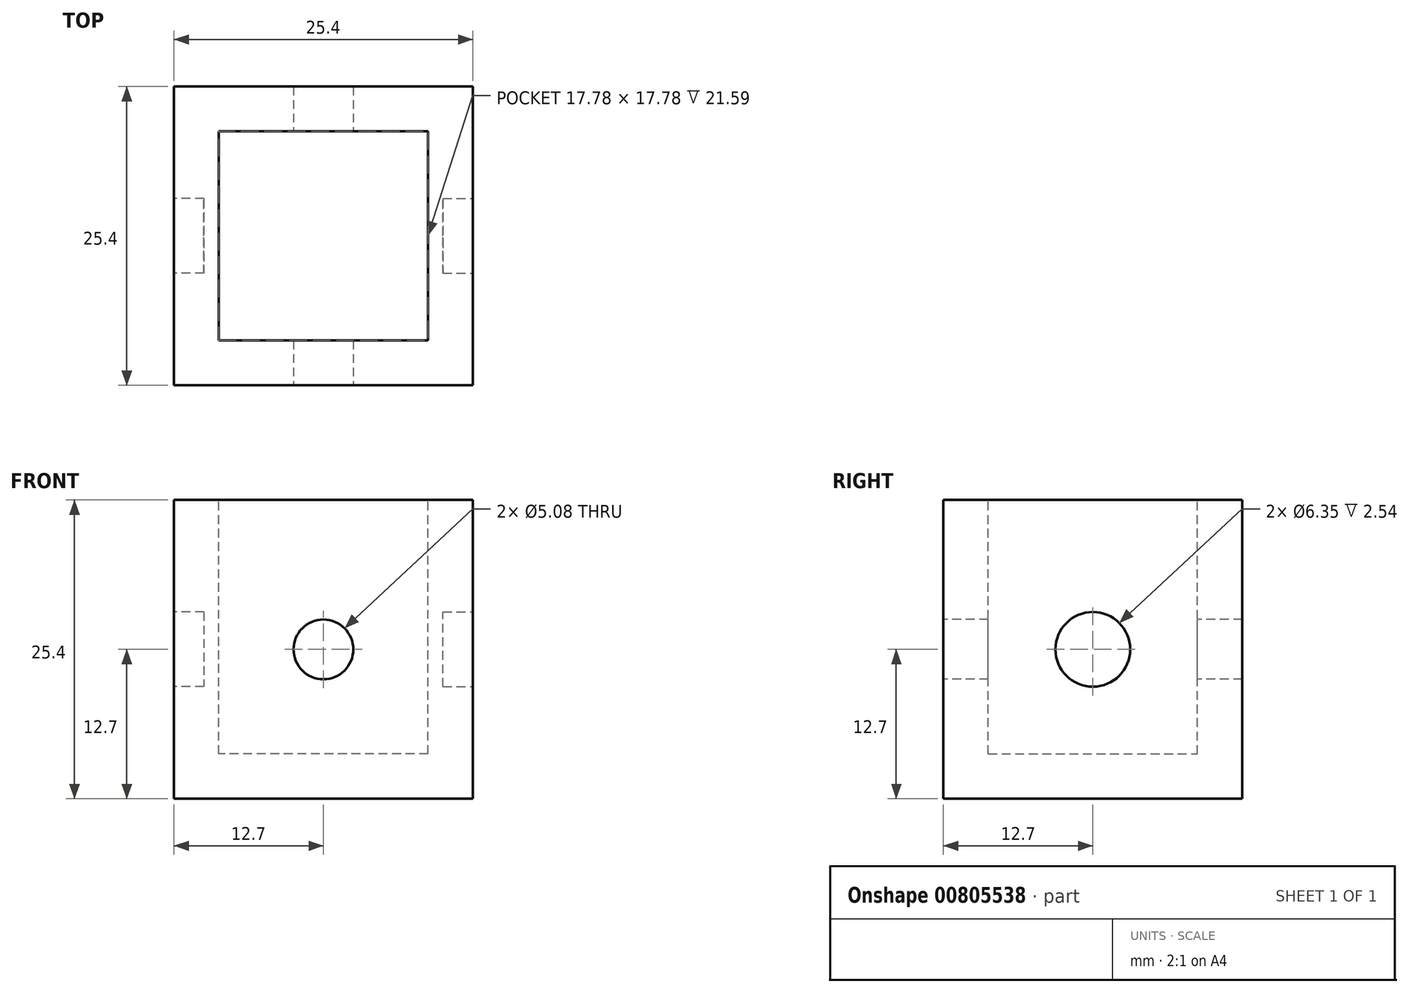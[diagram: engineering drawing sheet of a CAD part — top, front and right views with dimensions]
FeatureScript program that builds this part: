
annotation { "Feature Type Name" : "Feature", "Feature Type Description" : "" }
export const myFeature = defineFeature(function(context is Context, id is Id, definition is map)
    precondition{}
    {
        {
            var Q0;
            Q0=qCreatedBy(makeId("Front.planeOp"),FACE);
            var sketch = newSketch(context, id + "F0", { "sketchPlane" : qUnion([Q0])});
            skLineSegment(sketch, "E0.bottom", {"start": v(0, 0) * mm, "end": v(-25.4, 0) * mm});
            skLineSegment(sketch, "E0.top", {"start": v(0, 25.4) * mm, "end": v(-25.4, 25.4) * mm});
            skLineSegment(sketch, "E0.left", {"start": v(0, 0) * mm, "end": v(0, 25.4) * mm});
            skLineSegment(sketch, "E0.right", {"start": v(-25.4, 0) * mm, "end": v(-25.4, 25.4) * mm});
            skSolve(sketch);
        }
        {
            var Q0;
            Q0 = qSketchRegion(id + "F0", true);
            extrude(context, id + "F1", {"entities" : qUnion([Q0]), "depth" : 25.4 * mm, "offsetDistance" : 25.4 * mm});
        }
        {
            var Q0;
            Q0=makeQuery(id+"F1.opExtrude","SWEPT_FACE",FACE,{"disambiguationData":[OSD([sQuery(id+"F0.wireOp",EDGE,"E0.top")])]});
            shell(context, id + "F2", {"entities" : qUnion([Q0]), "thickness" : 3.8 * mm});
        }
        {
            var Q0;
            Q0=makeQuery(id+"F1.opExtrude","CAP_FACE",FACE,{"disambiguationData":[OSD([sQuery(id+"F0.wireOp",EDGE,"E0.bottom"),sQuery(id+"F0.wireOp",EDGE,"E0.top"),sQuery(id+"F0.wireOp",EDGE,"E0.left"),sQuery(id+"F0.wireOp",EDGE,"E0.right")])],"isStart":false});
            var sketch = newSketch(context, id + "F3", { "sketchPlane" : qUnion([Q0])});
            skPoint(sketch, "E1", {"position": v(-12.7, 12.7) * mm});
            skSolve(sketch);
        }
        {
            var Q0;
            Q0=makeQuery(id+"F1.opExtrude","SWEPT_FACE",FACE,{"disambiguationData":[OSD([sQuery(id+"F0.wireOp",EDGE,"E0.left")])]});
            var sketch = newSketch(context, id + "F4", { "sketchPlane" : qUnion([Q0])});
            skPoint(sketch, "E2", {"position": v(-12.7, 12.7) * mm});
            skCircle(sketch, "E3", {"center": v(-12.7, 12.7) * mm, "radius": 3.18 * mm});
            skSolve(sketch);
        }
        {
            var Q0;
            Q0=sQuery(id+"F3.wireOp",VERTEX,"E1");
            var Q1;
            Q1=makeQuery(id+"F1.opExtrude","SWEPT_BODY",BODY,{"disambiguationData":[OSD([sQuery(id+"F0.wireOp",EDGE,"E0.bottom"),sQuery(id+"F0.wireOp",EDGE,"E0.top"),sQuery(id+"F0.wireOp",EDGE,"E0.left"),sQuery(id+"F0.wireOp",EDGE,"E0.right")])]});
            hole(context, id + "F5", {"style" : HoleStyle.SIMPLE, "endStyle" : HoleEndStyle.BLIND, "holeDiameter" : 5.08 * mm, "majorDiameter" : 6.35 * mm, "holeDepth" : 50.8 * mm, "isTappedThrough" : true, "tappedDepth" : 12.7 * mm, "tapClearance" : 3, "startFromSketch" : true, "locations" : qUnion([Q0]), "scope" : qUnion([Q1])});
        }
        {
            var Q0;
            Q0=makeQuery(id+"F4.imprint","IMPRINT",FACE,{"disambiguationData":[TD([[makeQuery(id+"F4.imprint","IMPRINT",EDGE,{"derivedFrom":sQuery(id+"F4.wireOp",EDGE,"E3")}),1.0]])]});
            extrude(context, id + "F6", {"entities" : qUnion([Q0]), "operationType" : NewBodyOperationType.REMOVE, "oppositeDirection" : true, "depth" : 2.54 * mm, "offsetDistance" : 25.4 * mm});
        }
        {
            var Q0;
            Q0=makeQuery(id+"F1.opExtrude","SWEPT_FACE",FACE,{"disambiguationData":[OSD([sQuery(id+"F0.wireOp",EDGE,"E0.right")])]});
            var sketch = newSketch(context, id + "F7", { "sketchPlane" : qUnion([Q0])});
            skPoint(sketch, "E4", {"position": v(12.7, 12.7) * mm});
            skCircle(sketch, "E5", {"center": v(12.7, 12.7) * mm, "radius": 3.18 * mm});
            skSolve(sketch);
        }
        {
            var Q0;
            Q0=makeQuery(id+"F7.imprint","IMPRINT",FACE,{"disambiguationData":[TD([[makeQuery(id+"F7.imprint","IMPRINT",EDGE,{"derivedFrom":sQuery(id+"F7.wireOp",EDGE,"E5")}),1.0]])]});
            extrude(context, id + "F8", {"entities" : qUnion([Q0]), "operationType" : NewBodyOperationType.REMOVE, "oppositeDirection" : true, "depth" : 2.54 * mm, "offsetDistance" : 25.4 * mm});
        }
    });
